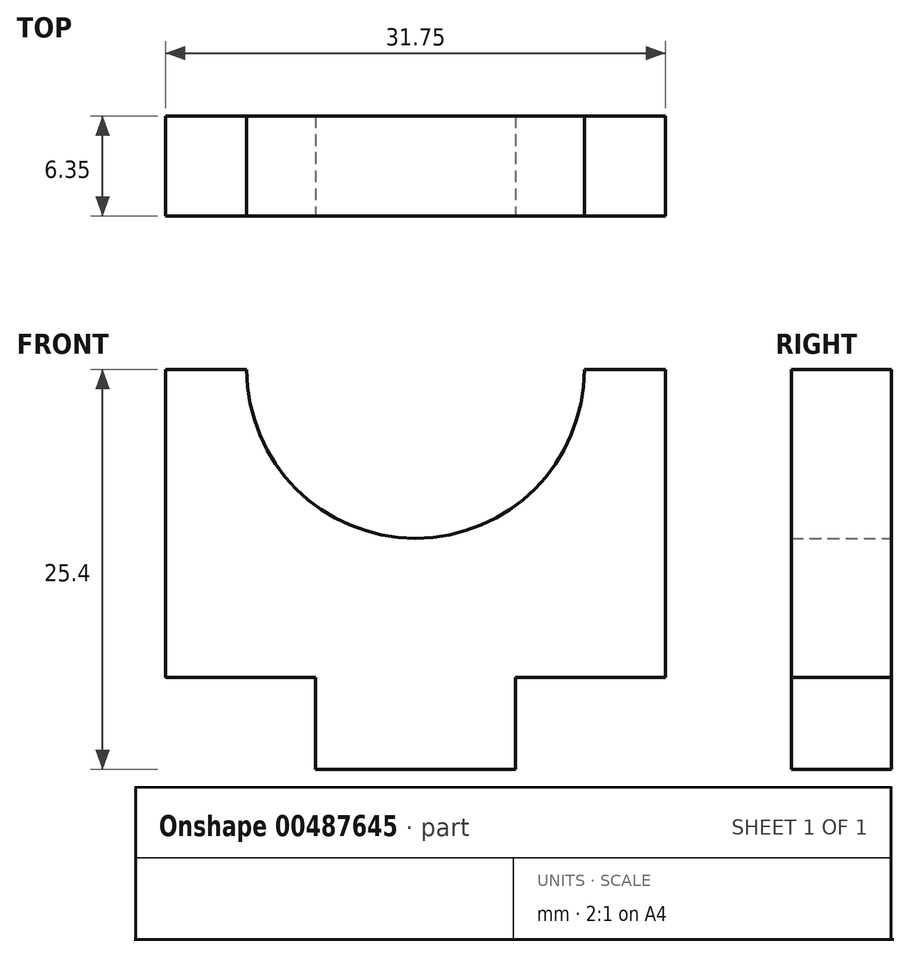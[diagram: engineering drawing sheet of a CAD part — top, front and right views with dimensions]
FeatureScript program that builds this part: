
annotation { "Feature Type Name" : "Feature", "Feature Type Description" : "" }
export const myFeature = defineFeature(function(context is Context, id is Id, definition is map)
    precondition{}
    {
        {
            var Q0;
            Q0=qCreatedBy(makeId("Front.planeOp"),FACE);
            var sketch = newSketch(context, id + "F0", { "sketchPlane" : qUnion([Q0])});
            skLineSegment(sketch, "E0.bottom", {"start": v(0, 0) * mm, "end": v(31.75, 0) * mm});
            skLineSegment(sketch, "E0.top", {"start": v(0, 25.4) * mm, "end": v(31.75, 25.4) * mm});
            skLineSegment(sketch, "E0.left", {"start": v(0, 0) * mm, "end": v(0, 25.4) * mm});
            skLineSegment(sketch, "E0.right", {"start": v(31.75, 0) * mm, "end": v(31.75, 25.4) * mm});
            skSolve(sketch);
        }
        {
            var Q0;
            Q0 = qSketchRegion(id + "F0", true);
            extrude(context, id + "F1", {"entities" : qUnion([Q0]), "depth" : 6.35 * mm});
        }
        {
            var Q0;
            Q0=makeQuery(id+"F1.opExtrude","CAP_FACE",FACE,{"disambiguationData":[OSD([sQuery(id+"F0.wireOp",EDGE,"E0.bottom"),sQuery(id+"F0.wireOp",EDGE,"E0.top"),sQuery(id+"F0.wireOp",EDGE,"E0.left"),sQuery(id+"F0.wireOp",EDGE,"E0.right")])],"isStart":true});
            var sketch = newSketch(context, id + "F2", { "sketchPlane" : qUnion([Q0])});
            skLineSegment(sketch, "E1", {"start": v(-26.6, 25.4) * mm, "end": v(-26.6, 0) * mm, "construction": true});
            skLineSegment(sketch, "E2", {"start": v(-5.16, 25.4) * mm, "end": v(-5.16, 0) * mm, "construction": true});
            skLineSegment(sketch, "E3", {"start": v(-31.75, 14.68) * mm, "end": v(0, 14.68) * mm, "construction": true});
            skArc(sketch, "E4", {"start": v(-26.6, 25.4) * mm, "mid": v(-15.88, 14.68) * mm, "end": v(-5.16, 25.4) * mm});
            skLineSegment(sketch, "E5", {"start": v(-26.6, 25.4) * mm, "end": v(-26.6, 28.93) * mm});
            skLineSegment(sketch, "E6", {"start": v(-26.6, 28.93) * mm, "end": v(-5.14, 28.93) * mm});
            skLineSegment(sketch, "E7", {"start": v(-5.14, 28.93) * mm, "end": v(-5.16, 25.4) * mm});
            skSolve(sketch);
        }
        {
            var Q0;
            Q0 = qSketchRegion(id + "F2", true);
            extrude(context, id + "F3", {"entities" : qUnion([Q0]), "operationType" : NewBodyOperationType.REMOVE, "oppositeDirection" : true, "depth" : 6.35 * mm});
        }
        {
            var Q0;
            Q0=makeQuery(id+"F1.opExtrude","CAP_FACE",FACE,{"disambiguationData":[OSD([sQuery(id+"F0.wireOp",EDGE,"E0.bottom"),sQuery(id+"F0.wireOp",EDGE,"E0.top"),sQuery(id+"F0.wireOp",EDGE,"E0.left"),sQuery(id+"F0.wireOp",EDGE,"E0.right")])],"isStart":false});
            var sketch = newSketch(context, id + "F4", { "sketchPlane" : qUnion([Q0])});
            skLineSegment(sketch, "E8", {"start": v(9.53, 25.4) * mm, "end": v(9.53, 0) * mm, "construction": true});
            skLineSegment(sketch, "E9", {"start": v(0, 5.84) * mm, "end": v(31.75, 5.84) * mm, "construction": true});
            skLineSegment(sketch, "E10", {"start": v(22.23, 25.81) * mm, "end": v(22.23, 0) * mm, "construction": true});
            skLineSegment(sketch, "E11.bottom", {"start": v(0, 5.84) * mm, "end": v(9.53, 5.84) * mm});
            skLineSegment(sketch, "E11.top", {"start": v(0, -1.01) * mm, "end": v(9.53, -1.01) * mm});
            skLineSegment(sketch, "E11.left", {"start": v(0, 5.84) * mm, "end": v(0, -1.01) * mm});
            skLineSegment(sketch, "E11.right", {"start": v(9.53, 5.84) * mm, "end": v(9.53, -1.01) * mm});
            skLineSegment(sketch, "E12.bottom", {"start": v(22.23, 5.84) * mm, "end": v(31.75, 5.84) * mm});
            skLineSegment(sketch, "E12.top", {"start": v(22.23, -1.01) * mm, "end": v(31.75, -1.01) * mm});
            skLineSegment(sketch, "E12.left", {"start": v(22.23, 5.84) * mm, "end": v(22.23, -1.01) * mm});
            skLineSegment(sketch, "E12.right", {"start": v(31.75, 5.84) * mm, "end": v(31.75, -1.01) * mm});
            skSolve(sketch);
        }
        {
            var Q0;
            Q0 = qSketchRegion(id + "F4", true);
            extrude(context, id + "F5", {"entities" : qUnion([Q0]), "operationType" : NewBodyOperationType.REMOVE, "endBound" : BoundingType.THROUGH_ALL, "oppositeDirection" : true, "depth" : 25.4 * mm});
        }
    });
